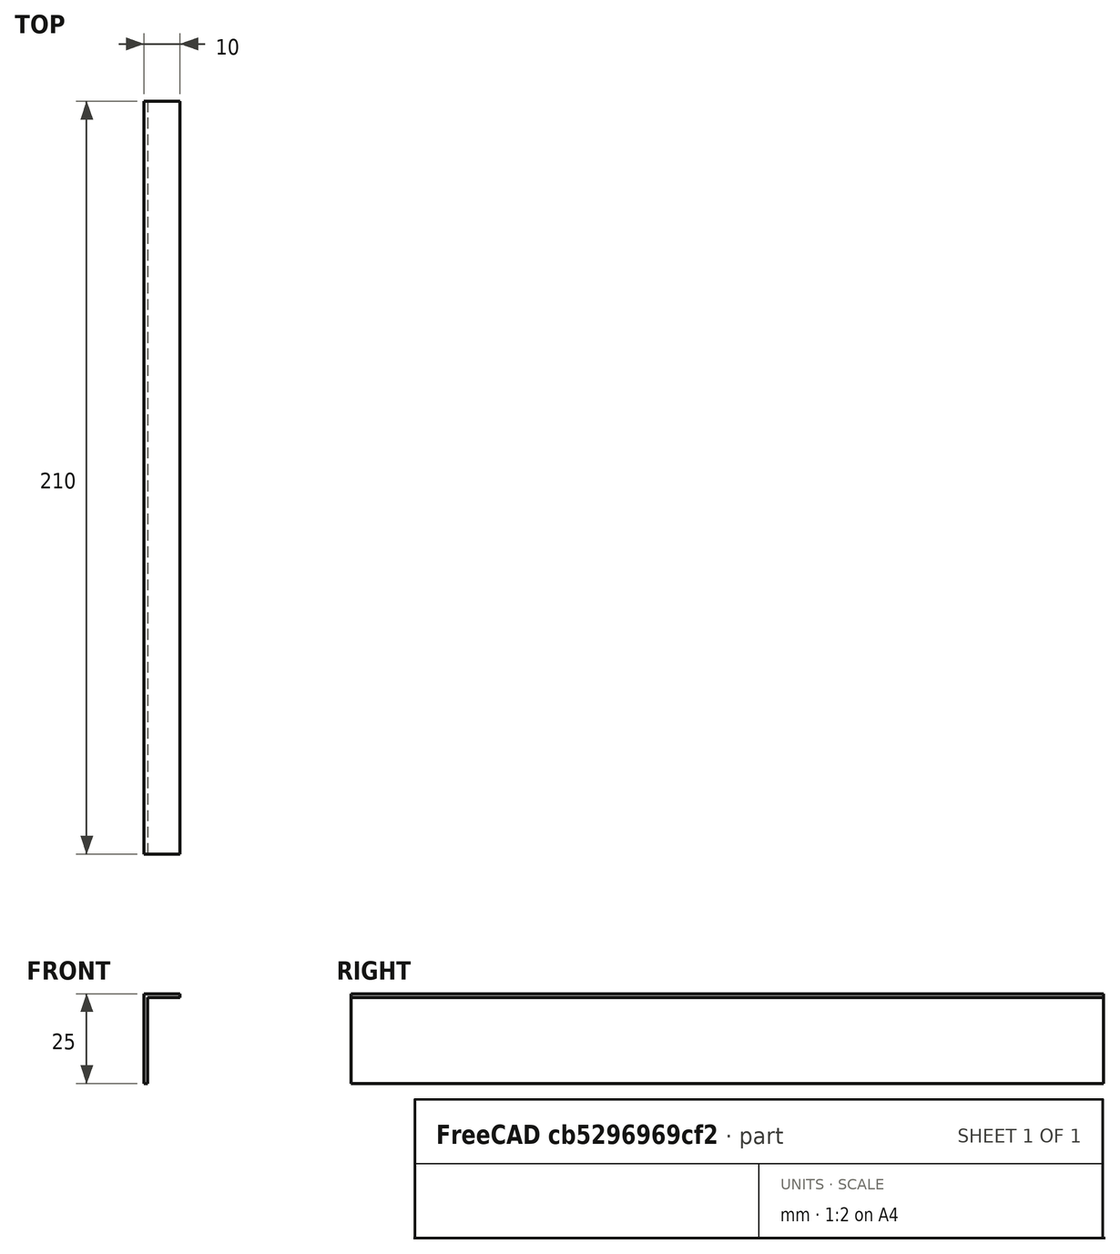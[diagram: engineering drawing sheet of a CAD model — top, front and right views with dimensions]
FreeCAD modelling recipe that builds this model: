
FCSTD DOCUMENT  (FreeCAD 0.21R33694 (Git))
Label: baguette-info-tirettes-ua
License: Creative Commons Attribution 3.0
LicenseURL: http://en.wikipedia.org/wiki/Public_domain
objects: Sketcher::SketchObject×1, PartDesign::Pad×1, PartDesign::Body×1
note: 4 computed .brp shape members not serialized (recipe doc carries the construction recipe); baked Part::Feature solids carry a one-line shape summary decoded from their .brp

FEATURE [Sketcher::SketchObject] Sketch
  FullyConstrained = true
  MapMode = 5
  Placement = pos=(0,0,0) rot=(1,0,0;1.5708rad)
  Support = -> [XZ_Plane]
  sketch-geometry (6):
    g0: LineSegment StartX=9 StartY=0 StartZ=0 EndX=0 EndY=0 EndZ=0
    g1: LineSegment StartX=0 StartY=0 StartZ=0 EndX=0 EndY=-24 EndZ=0
    g2: LineSegment StartX=0 StartY=-24 StartZ=0 EndX=-1 EndY=-24 EndZ=0
    g3: LineSegment StartX=-1 StartY=-24 StartZ=0 EndX=-1 EndY=1 EndZ=0
    g4: LineSegment StartX=-1 StartY=1 StartZ=0 EndX=9 EndY=1 EndZ=0
    g5: LineSegment StartX=9 StartY=1 StartZ=0 EndX=9 EndY=0 EndZ=0
  constraints (17):
    c: PointOnObject(g0,g-1)
    c: Coincident(g0,g-1)
    c: Coincident(g0,g1)
    c: PointOnObject(g1,g-2)
    c: Coincident(g1,g2)
    c: Horizontal(g2)
    c: Coincident(g2,g3)
    c: Vertical(g3)
    c: Coincident(g3,g4)
    c: Horizontal(g4)
    c: Coincident(g4,g5)
    c: Coincident(g5,g0)
    c: Vertical(g5)
    c: DistanceY(g5,g5) = 1
    c: DistanceX(g2,g2) = 1
    c: DistanceX(g4,g4) = 10
    c: DistanceY(g3,g3) = 25
FEATURE [PartDesign::Pad] Pad
  Direction = (0,-1,2e-16)
  Length = 210
  Length2 = 10
  Placement = pos=(0,0,0) rot=(1,0,0;1.5708rad)
  Profile = -> Sketch
  ReferenceAxis = -> Sketch [N_Axis]
  Type = 0
FEATURE [PartDesign::Body] Body
  Group = -> [Sketch,Pad]
  Origin = -> Origin
  Tip = -> Pad
